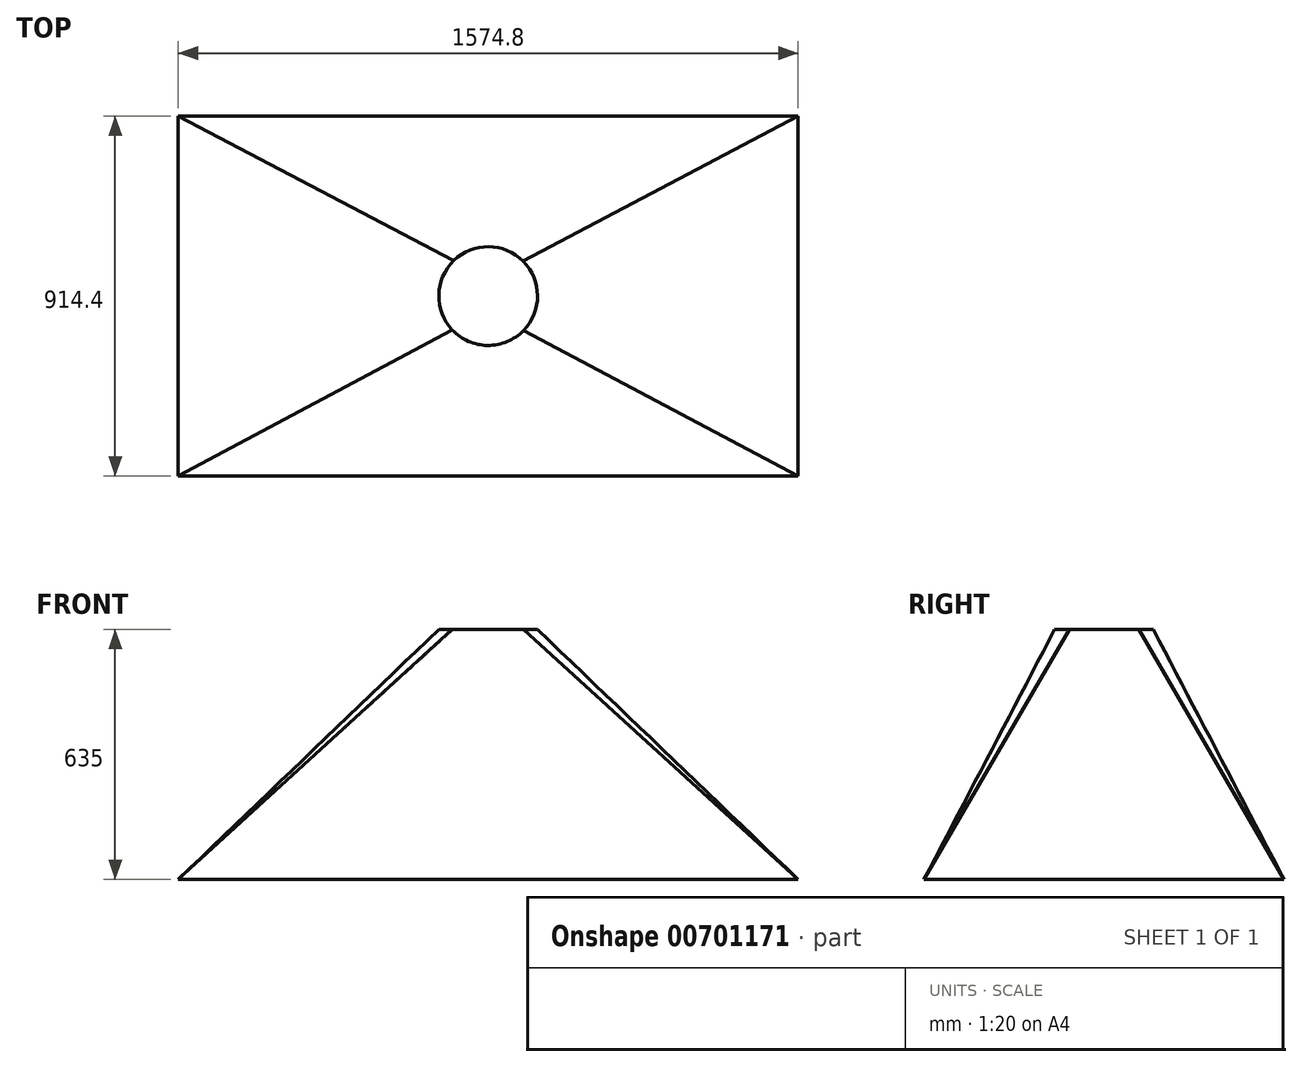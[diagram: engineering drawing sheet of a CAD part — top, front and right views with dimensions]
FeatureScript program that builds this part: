
annotation { "Feature Type Name" : "Feature", "Feature Type Description" : "" }
export const myFeature = defineFeature(function(context is Context, id is Id, definition is map)
    precondition{}
    {
        {
            var Q0;
            Q0=qCreatedBy(makeId("Top.planeOp"),FACE);
            var sketch = newSketch(context, id + "F0", { "sketchPlane" : qUnion([Q0])});
            skLineSegment(sketch, "E0.bottom", {"start": v(-787.4, 457.2) * mm, "end": v(787.4, 457.2) * mm});
            skLineSegment(sketch, "E0.top", {"start": v(-787.4, -457.2) * mm, "end": v(787.4, -457.2) * mm});
            skLineSegment(sketch, "E0.left", {"start": v(-787.4, 457.2) * mm, "end": v(-787.4, -457.2) * mm});
            skLineSegment(sketch, "E0.right", {"start": v(787.4, 457.2) * mm, "end": v(787.4, -457.2) * mm});
            skPoint(sketch, "E0.middle", {"position": v(0, 0) * mm});
            skSolve(sketch);
        }
        {
            var Q0;
            Q0=qCreatedBy(makeId("Top.planeOp"),FACE);
            cPlane(context, id + "F1", {"entities" : qUnion([Q0]), "cplaneType" : CPlaneType.OFFSET, "offset" : 635 * mm, "width" : 152.4 * mm, "height" : 152.4 * mm});
        }
        {
            var Q0;
            Q0=qCreatedBy(id+"F1.planeOp",FACE);
            var sketch = newSketch(context, id + "F2", { "sketchPlane" : qUnion([Q0])});
            skCircle(sketch, "E1", {"center": v(0, 0) * mm, "radius": 127 * mm});
            skSolve(sketch);
        }
        {
            var Q0;
            Q0=qCreatedBy(id+"F1.planeOp",FACE);
            var sketch = newSketch(context, id + "F3", { "sketchPlane" : qUnion([Q0])});
            skArc(sketch, "E2", {"start": v(-87.52, 92.03) * mm, "mid": v(-2, -126.98) * mm, "end": v(90.36, 89.24) * mm});
            skArc(sketch, "E3", {"start": v(90.36, 89.24) * mm, "mid": v(2, 126.98) * mm, "end": v(-87.52, 92.03) * mm});
            skArc(sketch, "E4", {"start": v(-91.17, -86.12) * mm, "mid": v(-1.06, -125.4) * mm, "end": v(89.7, -87.65) * mm});
            skArc(sketch, "E5", {"start": v(89.7, -87.65) * mm, "mid": v(1.06, 125.4) * mm, "end": v(-91.17, -86.12) * mm});
            skSolve(sketch);
        }
        {
            var Q0;
            Q0=makeQuery(id+"F3.imprint","IMPRINT",FACE,{"disambiguationData":[TD([[makeQuery(id+"F3.imprint","IMPRINT",EDGE,{"derivedFrom":sQuery(id+"F3.wireOp",EDGE,"E4")}),1.0]])]});
            var Q1;
            Q1=makeQuery(id+"F0.imprint","IMPRINT",FACE,{"disambiguationData":[TD([[makeQuery(id+"F0.imprint","IMPRINT",EDGE,{"derivedFrom":sQuery(id+"F0.wireOp",EDGE,"E0.bottom")}),-1.0]])]});
            loft(context, id + "F4", {"sheetProfilesArray" : [{ "sheetProfileEntities" : qUnion([Q0]) }, { "sheetProfileEntities" : qUnion([Q1]) }]});
        }
    });
